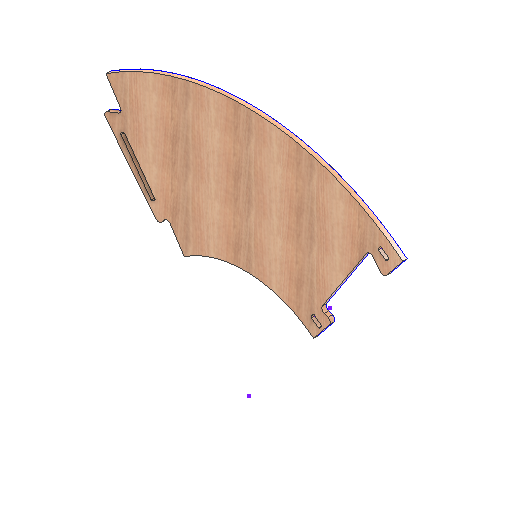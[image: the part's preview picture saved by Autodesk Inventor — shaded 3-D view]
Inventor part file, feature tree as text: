
AUTODESK INVENTOR PART (.ipt)
format: ipt  version: 2021 (Build 250183000, 183)  size: 235,008 bytes
history: native  units: mm
features: other x2, extrude x2, hole x1
ambient origin geometry x8: Origin, YZ Plane, XZ Plane, XY Plane, X Axis, Y Axis, Z Axis, Center Point
bodies: Solid1 (feature_tree)
feature tree (5):
  other  "CONTOURS"
  hole  "HOLES"  [1 undecoded]
  other  "LETTERS"
  extrude  "Extrusion3"  Depth=18.0mm TaperAngle=0.0deg
  extrude  "Extrusion4"  [1 undecoded]
note: 2 required parameter values undecoded (feature->parameter linkage not recoverable at this tier; creation-order binding heuristic only, values carry confidence <= 0.55)
